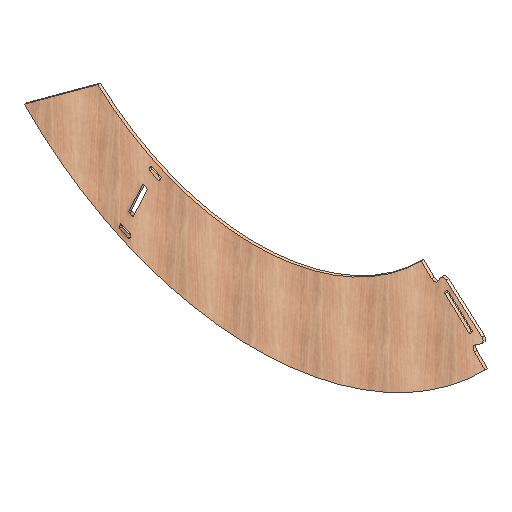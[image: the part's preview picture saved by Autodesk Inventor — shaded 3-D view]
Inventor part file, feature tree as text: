
AUTODESK INVENTOR PART (.ipt)
format: ipt  version: 2021 (Build 250183000, 183)  size: 386,048 bytes
history: native  units: mm
features: other x2, extrude x2, hole x1
ambient origin geometry x8: Origin, YZ Plane, XZ Plane, XY Plane, X Axis, Y Axis, Z Axis, Center Point
bodies: Solid1 (feature_tree)
feature tree (5):
  other  "CONTOURS"
  hole  "HOLES"  [1 undecoded]
  other  "LETTERS"
  extrude  "Extrusion1"  Depth=16.688506mm
  extrude  "Extrusion2"  Depth=18.0mm
note: 1 required parameter value undecoded (feature->parameter linkage not recoverable at this tier; creation-order binding heuristic only, values carry confidence <= 0.55)
